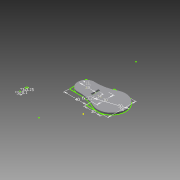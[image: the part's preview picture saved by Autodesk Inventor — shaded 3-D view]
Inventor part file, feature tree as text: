
AUTODESK INVENTOR PART (.ipt)
format: ipt  version: 2013 (Build 170138000, 138)  size: 123,904 bytes
history: native  units: mm
features: extrude x3, other x2, sketch x1
ambient origin geometry x8: Origin, YZ Plane, XZ Plane, XY Plane, X Axis, Y Axis, Z Axis, Center Point
feature tree (6):
  other  "Blocks"
  sketch  "Sketch1"  dims[d0=3.0mm d2=3.0mm d3=0.1mm d7=22.5mm d8=12.4mm d9=4.5mm d10=4.5mm d11=2.0mm d12=2.0mm d23=40.0mm d24=30.0mm d29=3.25mm d30=14.0mm d31=30.0mm d38=30.0mm d39=50.0mm d42=13.0mm d43=50.0mm d44=3.25mm d45=0.0mm d46=3.25mm d47=0.0mm d48=3.25mm d49=0.0mm]
  extrude  "Extrusion6"  Depth=3.0mm
  extrude  "Extrusion7"  Depth=40.0mm
  extrude  "Extrusion8"  Depth=30.0mm
  other  "Block1"
